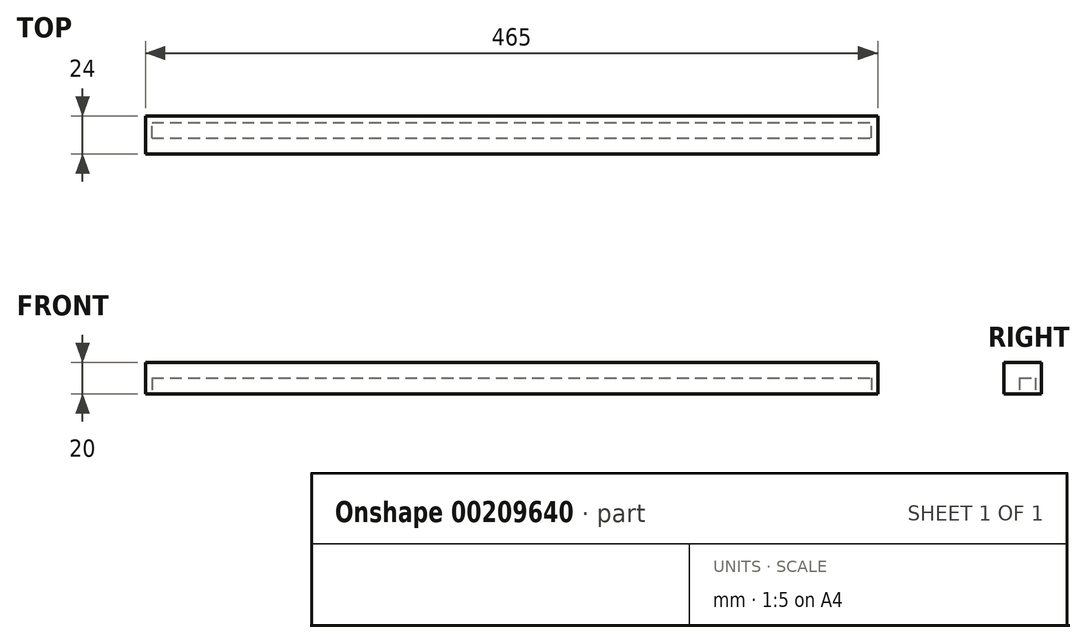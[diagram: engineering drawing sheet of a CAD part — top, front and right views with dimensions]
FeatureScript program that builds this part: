
annotation { "Feature Type Name" : "Feature", "Feature Type Description" : "" }
export const myFeature = defineFeature(function(context is Context, id is Id, definition is map)
    precondition{}
    {
        {
            var Q0;
            Q0=qCreatedBy(makeId("Top.planeOp"),FACE);
            var sketch = newSketch(context, id + "F0", { "sketchPlane" : qUnion([Q0])});
            skLineSegment(sketch, "E0.bottom", {"start": v(19.54, -50.04) * mm, "end": v(484.54, -50.04) * mm});
            skLineSegment(sketch, "E0.top", {"start": v(19.54, -32.04) * mm, "end": v(484.54, -32.04) * mm});
            skLineSegment(sketch, "E0.left", {"start": v(19.54, -50.04) * mm, "end": v(19.54, -32.04) * mm});
            skLineSegment(sketch, "E0.right", {"start": v(484.54, -50.04) * mm, "end": v(484.54, -32.04) * mm});
            skLineSegment(sketch, "E1.0", {"start": v(23.54, -46.04) * mm, "end": v(480.54, -46.04) * mm});
            skLineSegment(sketch, "E1.1", {"start": v(23.54, -46.04) * mm, "end": v(23.54, -36.04) * mm});
            skLineSegment(sketch, "E1.2", {"start": v(23.54, -36.04) * mm, "end": v(480.54, -36.04) * mm});
            skLineSegment(sketch, "E1.3", {"start": v(480.54, -46.04) * mm, "end": v(480.54, -36.04) * mm});
            skLineSegment(sketch, "E2.top", {"start": v(19.54, -56.04) * mm, "end": v(484.54, -56.04) * mm});
            skLineSegment(sketch, "E2.left", {"start": v(19.54, -50.04) * mm, "end": v(19.54, -56.04) * mm});
            skLineSegment(sketch, "E2.right", {"start": v(484.54, -50.04) * mm, "end": v(484.54, -56.04) * mm});
            skSolve(sketch);
        }
        {
            var Q0;
            Q0=makeQuery(id+"F0.imprint","IMPRINT",FACE,{"disambiguationData":[TD([[makeQuery(id+"F0.imprint","IMPRINT",EDGE,{"derivedFrom":sQuery(id+"F0.wireOp",EDGE,"E0.bottom")}),1.0]])]});
            var Q1;
            Q1=makeQuery(id+"F0.imprint","IMPRINT",FACE,{"disambiguationData":[TD([[makeQuery(id+"F0.imprint","IMPRINT",EDGE,{"derivedFrom":sQuery(id+"F0.wireOp",EDGE,"E0.bottom")}),-1.0]])]});
            var Q2;
            Q2=makeQuery(id+"F0.imprint","IMPRINT",FACE,{"disambiguationData":[TD([[makeQuery(id+"F0.imprint","IMPRINT",EDGE,{"derivedFrom":sQuery(id+"F0.wireOp",EDGE,"E0.top")}),-1.0]])]});
            extrude(context, id + "F1", {"entities" : qUnion([Q0, Q1, Q2]), "depth" : 20 * mm});
        }
        {
            var Q0;
            Q0=makeQuery(id+"F0.imprint","IMPRINT",FACE,{"disambiguationData":[TD([[makeQuery(id+"F0.imprint","IMPRINT",EDGE,{"derivedFrom":sQuery(id+"F0.wireOp",EDGE,"E1.0")}),1.0]])]});
            extrude(context, id + "F2", {"entities" : qUnion([Q0]), "operationType" : NewBodyOperationType.ADD, "depth" : 20 * mm, "hasSecondDirection" : true, "secondDirectionOppositeDirection" : false, "secondDirectionDepth" : 10 * mm});
        }
    });
